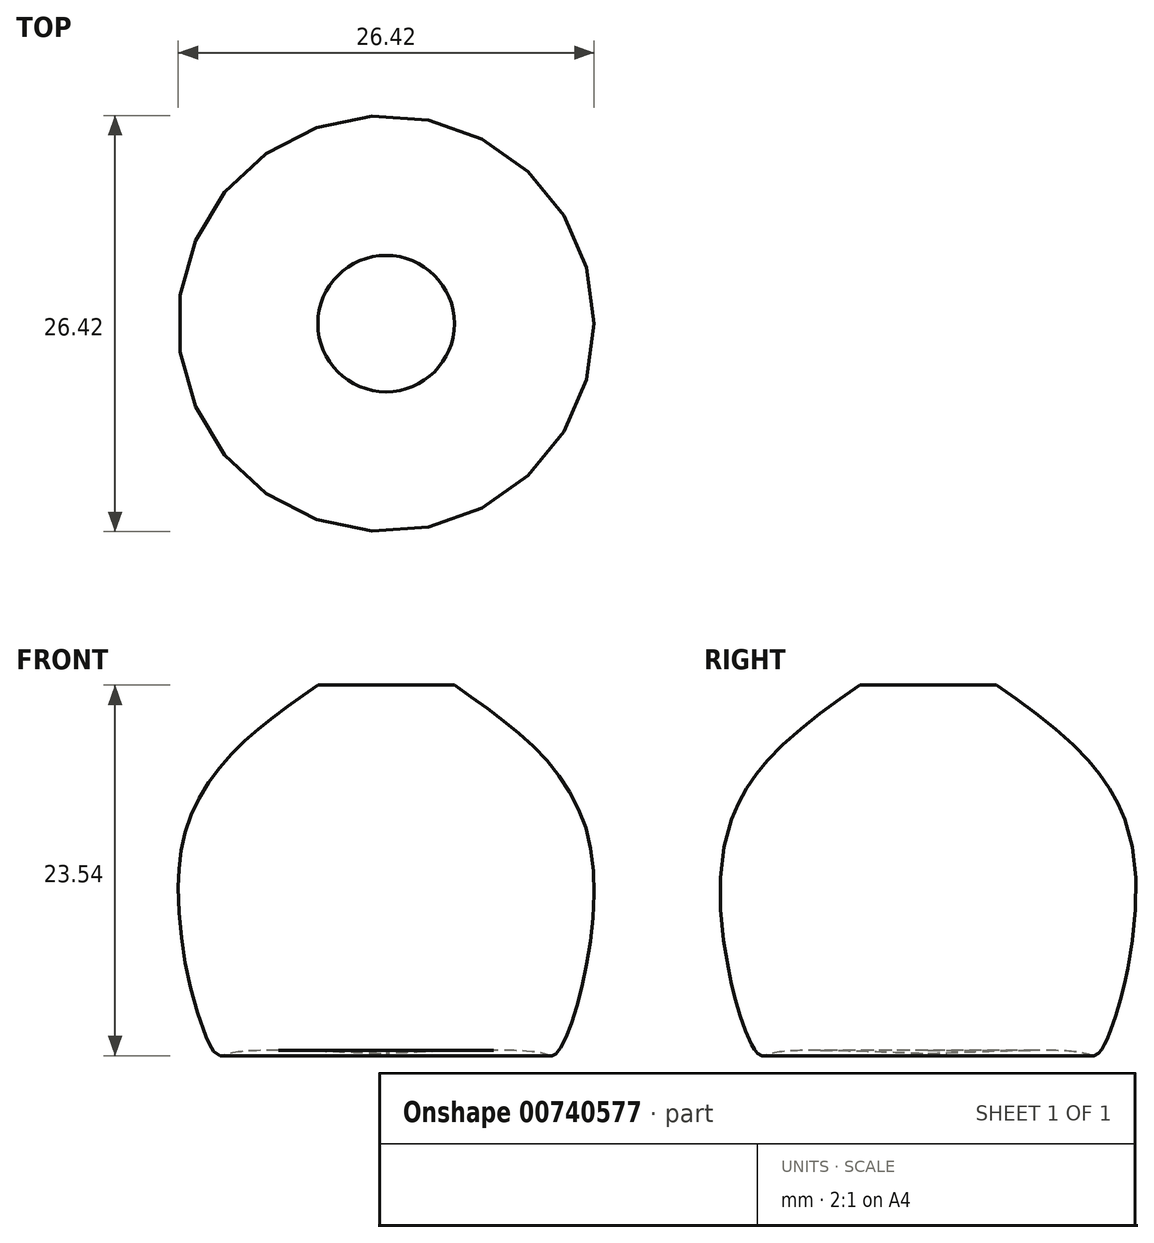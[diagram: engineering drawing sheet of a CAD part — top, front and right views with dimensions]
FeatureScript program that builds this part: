
annotation { "Feature Type Name" : "Feature", "Feature Type Description" : "" }
export const myFeature = defineFeature(function(context is Context, id is Id, definition is map)
    precondition{}
    {
        {
            var Q0;
            Q0=qCreatedBy(makeId("Front.planeOp"),FACE);
            var sketch = newSketch(context, id + "F0", { "sketchPlane" : qUnion([Q0])});
            skLineSegment(sketch, "E0", {"start": v(0, 0) * mm, "end": v(0, 23.4) * mm});
            skLineSegment(sketch, "E1", {"start": v(0, 23.4) * mm, "end": v(4.33, 23.4) * mm});
            skFitSpline(sketch, "E2", {"points": [v(4.33, 23.4) * mm, v(13, 13) * mm, v(10.83, 0) * mm, v(9.97, 0) * mm, v(0, 0) * mm], "startDerivative": vector(36.15, -25.21) * mm, "endDerivative": vector(-46.1, -1.9) * mm});
            skSolve(sketch);
        }
        {
            var Q0;
            Q0=makeQuery(id+"F0.imprint","IMPRINT",FACE,{"disambiguationData":[TD([[makeQuery(id+"F0.imprint","IMPRINT",EDGE,{"derivedFrom":sQuery(id+"F0.wireOp",EDGE,"E0")}),-1.0]])]});
            var Q1;
            Q1=sQuery(id+"F0.wireOp",EDGE,"E0");
            revolve(context, id + "F1", {"surfaceOperationType" : NewSurfaceOperationType.NEW, "entities" : qUnion([Q0]), "axis" : qUnion([Q1]), "revolveType" : RevolveType.FULL});
        }
    });
